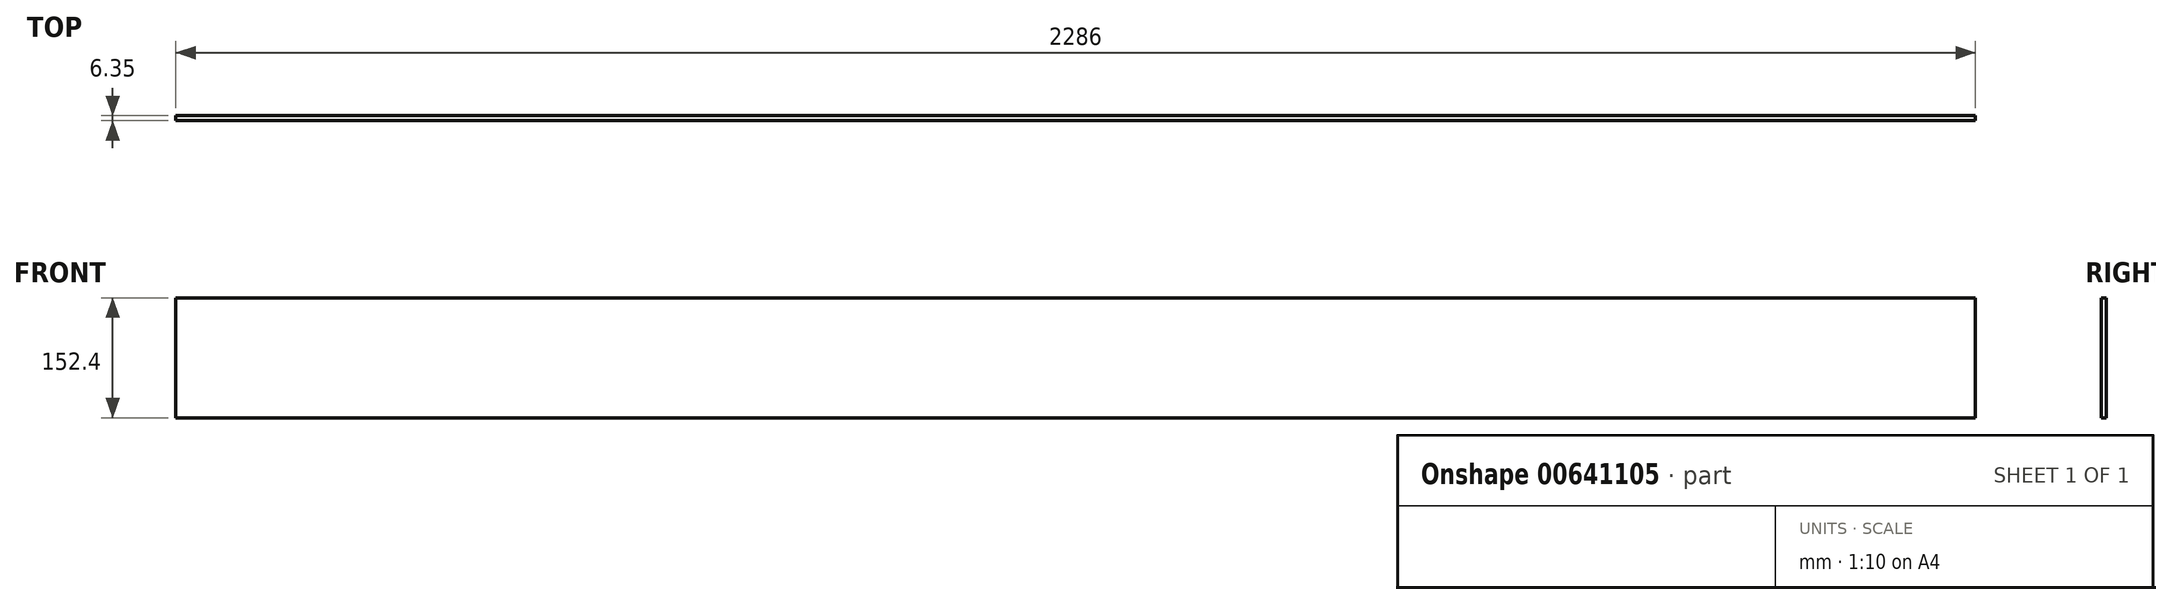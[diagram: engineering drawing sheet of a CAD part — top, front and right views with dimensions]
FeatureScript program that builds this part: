
annotation { "Feature Type Name" : "Feature", "Feature Type Description" : "" }
export const myFeature = defineFeature(function(context is Context, id is Id, definition is map)
    precondition{}
    {
        {
            var Q0;
            Q0=qCreatedBy(makeId("Front.planeOp"),FACE);
            var sketch = newSketch(context, id + "F0", { "sketchPlane" : qUnion([Q0])});
            skLineSegment(sketch, "E0.bottom", {"start": v(-1146.31, -119.7) * mm, "end": v(1139.69, -119.7) * mm});
            skLineSegment(sketch, "E0.top", {"start": v(-1146.31, -272.1) * mm, "end": v(1139.69, -272.1) * mm});
            skLineSegment(sketch, "E0.left", {"start": v(-1146.31, -119.7) * mm, "end": v(-1146.31, -272.1) * mm});
            skLineSegment(sketch, "E0.right", {"start": v(1139.69, -119.7) * mm, "end": v(1139.69, -272.1) * mm});
            skSolve(sketch);
        }
        {
            var Q0;
            Q0=makeQuery(id+"F0.imprint","IMPRINT",FACE,{"disambiguationData":[TD([[makeQuery(id+"F0.imprint","IMPRINT",EDGE,{"derivedFrom":sQuery(id+"F0.wireOp",EDGE,"E0.bottom")}),-1.0]])]});
            extrude(context, id + "F1", {"entities" : qUnion([Q0]), "depth" : 6.35 * mm, "offsetDistance" : 25.4 * mm});
        }
    });
